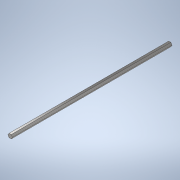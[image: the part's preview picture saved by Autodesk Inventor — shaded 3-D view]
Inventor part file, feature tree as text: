
AUTODESK INVENTOR PART (.ipt)
format: ipt  version: 2020 (Build 240168000, 168)  size: 105,984 bytes
history: native  units: in
note: dims shown in document units (in); Inventor stores cm internally (conversion verified against a paired STEP export)
features: extrude x1, sketch x1
ambient origin geometry x8: Origin, YZ Plane, XZ Plane, XY Plane, X Axis, Y Axis, Z Axis, Center Point
bodies: Solid1 (feature_tree)
feature tree (2):
  extrude  "Extrusion1"  Depth=21.0in TaperAngle=0.0deg
  sketch  "Sketch1"  dims[d0=0.5in d1=21.0in d2=0.0in]
